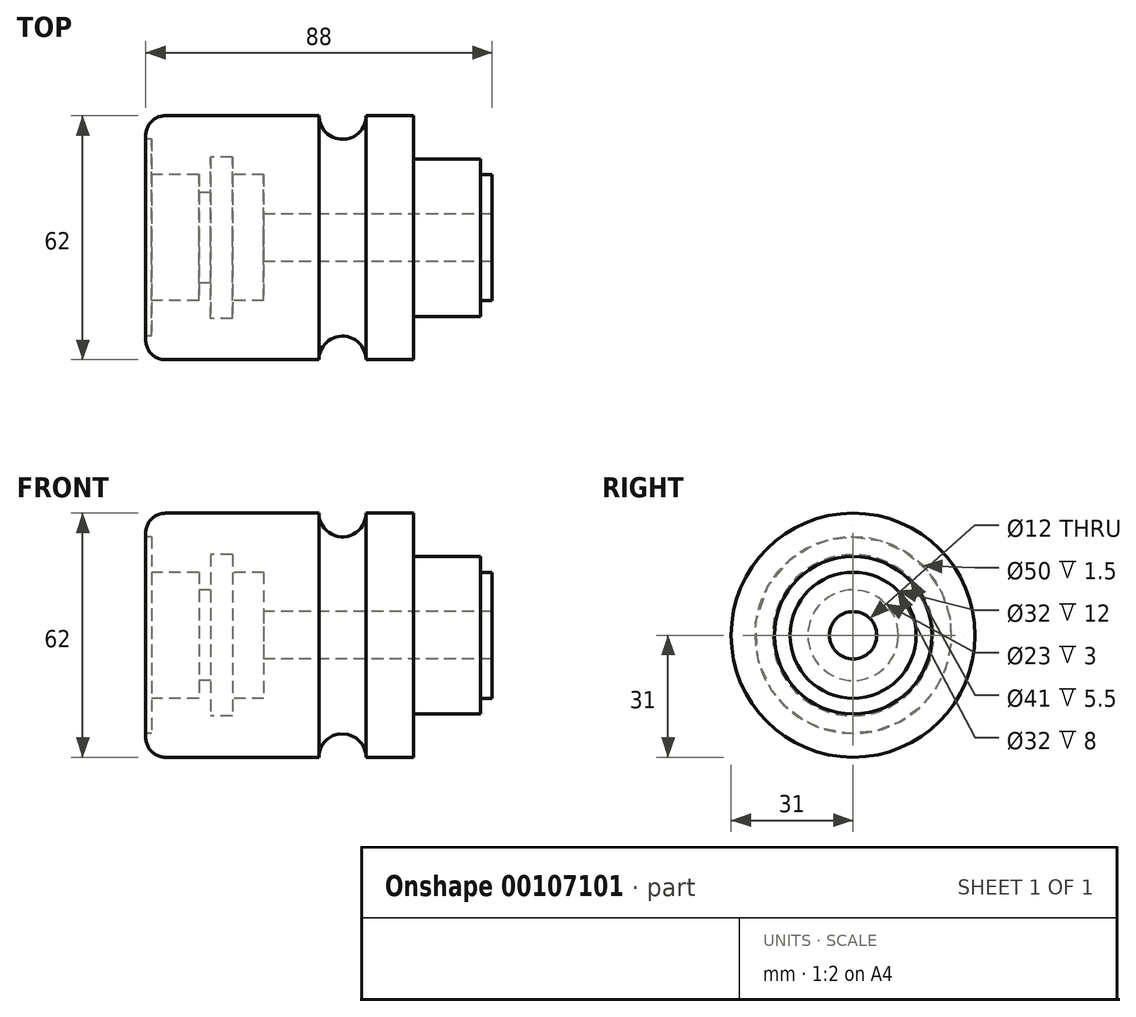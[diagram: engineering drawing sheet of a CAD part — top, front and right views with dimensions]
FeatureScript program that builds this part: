
annotation { "Feature Type Name" : "Feature", "Feature Type Description" : "" }
export const myFeature = defineFeature(function(context is Context, id is Id, definition is map)
    precondition{}
    {
        {
            var Q0;
            Q0=qCreatedBy(makeId("Front.planeOp"),FACE);
            var sketch = newSketch(context, id + "F0", { "sketchPlane" : qUnion([Q0])});
            skLineSegment(sketch, "E0", {"start": v(0, 0) * mm, "end": v(88, 0) * mm});
            skLineSegment(sketch, "E1", {"start": v(88, 0) * mm, "end": v(88, 16) * mm});
            skLineSegment(sketch, "E2", {"start": v(88, 16) * mm, "end": v(85, 16) * mm});
            skLineSegment(sketch, "E3", {"start": v(85, 16) * mm, "end": v(85, 20) * mm});
            skLineSegment(sketch, "E4", {"start": v(85, 20) * mm, "end": v(68, 20) * mm});
            skLineSegment(sketch, "E5", {"start": v(68, 20) * mm, "end": v(68, 31) * mm});
            skLineSegment(sketch, "E6", {"start": v(68, 31) * mm, "end": v(56, 31) * mm});
            skLineSegment(sketch, "E7", {"start": v(0, 26) * mm, "end": v(0, 0) * mm});
            skPoint(sketch, "E8.visualSharp", {"position": v(0, 31) * mm});
            skArc(sketch, "E8.filletArc", {"start": v(5, 31) * mm, "mid": v(1.46, 29.54) * mm, "end": v(0, 26) * mm});
            skArc(sketch, "E9", {"start": v(44, 31) * mm, "mid": v(50, 25) * mm, "end": v(56, 31) * mm});
            skLineSegment(sketch, "E10.trimOffspring", {"start": v(44, 31) * mm, "end": v(5, 31) * mm});
            skLineSegment(sketch, "E11", {"start": v(-7.73, 0) * mm, "end": v(117.4, 0) * mm, "construction": true});
            skPoint(sketch, "E12.start.orphan", {"position": v(88, 4.76) * mm});
            skLineSegment(sketch, "E13", {"start": v(0, 25) * mm, "end": v(1.5, 25) * mm, "construction": true});
            skLineSegment(sketch, "E14", {"start": v(1.5, 25) * mm, "end": v(1.5, 16) * mm, "construction": true});
            skLineSegment(sketch, "E15", {"start": v(1.5, 16) * mm, "end": v(13.5, 16) * mm, "construction": true});
            skLineSegment(sketch, "E16", {"start": v(13.5, 16) * mm, "end": v(13.5, 11.5) * mm, "construction": true});
            skLineSegment(sketch, "E17", {"start": v(13.5, 11.5) * mm, "end": v(16.5, 11.5) * mm, "construction": true});
            skLineSegment(sketch, "E18", {"start": v(16.5, 11.5) * mm, "end": v(16.5, 20.5) * mm, "construction": true});
            skLineSegment(sketch, "E19", {"start": v(16.5, 20.5) * mm, "end": v(22, 20.5) * mm, "construction": true});
            skLineSegment(sketch, "E20", {"start": v(22, 20.5) * mm, "end": v(22, 16) * mm, "construction": true});
            skLineSegment(sketch, "E21", {"start": v(22, 16) * mm, "end": v(30, 16) * mm, "construction": true});
            skLineSegment(sketch, "E22", {"start": v(30, 16) * mm, "end": v(30, 6) * mm, "construction": true});
            skLineSegment(sketch, "E23", {"start": v(30, 6) * mm, "end": v(88, 6) * mm, "construction": true});
            skLineSegment(sketch, "E24", {"start": v(0, 0) * mm, "end": v(0, 25) * mm});
            skLineSegment(sketch, "E25", {"start": v(0, 25) * mm, "end": v(1.5, 25) * mm});
            skLineSegment(sketch, "E26", {"start": v(1.5, 16) * mm, "end": v(13.5, 16) * mm});
            skLineSegment(sketch, "E27", {"start": v(13.5, 11.5) * mm, "end": v(16.5, 11.5) * mm});
            skLineSegment(sketch, "E28", {"start": v(16.5, 20.5) * mm, "end": v(22, 20.5) * mm});
            skLineSegment(sketch, "E29", {"start": v(1.5, 25) * mm, "end": v(1.5, 16) * mm});
            skLineSegment(sketch, "E30", {"start": v(13.5, 16) * mm, "end": v(13.5, 11.5) * mm});
            skLineSegment(sketch, "E31", {"start": v(16.5, 20.5) * mm, "end": v(16.5, 11.5) * mm});
            skLineSegment(sketch, "E32", {"start": v(22, 20.5) * mm, "end": v(22, 16) * mm});
            skLineSegment(sketch, "E33", {"start": v(22, 16) * mm, "end": v(30, 16) * mm});
            skLineSegment(sketch, "E34", {"start": v(30, 16) * mm, "end": v(30, 6) * mm});
            skLineSegment(sketch, "E35", {"start": v(30, 6) * mm, "end": v(88, 6) * mm});
            skLineSegment(sketch, "E36", {"start": v(88, 0) * mm, "end": v(0, 0) * mm});
            skSolve(sketch);
        }
        {
            var Q0;
            {var subQ1=sQuery(id+"F0.wireOp",EDGE,"E2");Q0=makeQuery(id+"F0.imprint","IMPRINT",FACE,{"disambiguationData":[TD([[makeQuery(id+"F0.imprint","IMPRINT",EDGE,{"derivedFrom":subQ1}),1.0]])]});}
            var Q1;
            Q1=sQuery(id+"F0.wireOp",EDGE,"E11");
            revolve(context, id + "F1", {"entities" : qUnion([Q0]), "axis" : qUnion([Q1]), "revolveType" : RevolveType.FULL});
        }
    });
